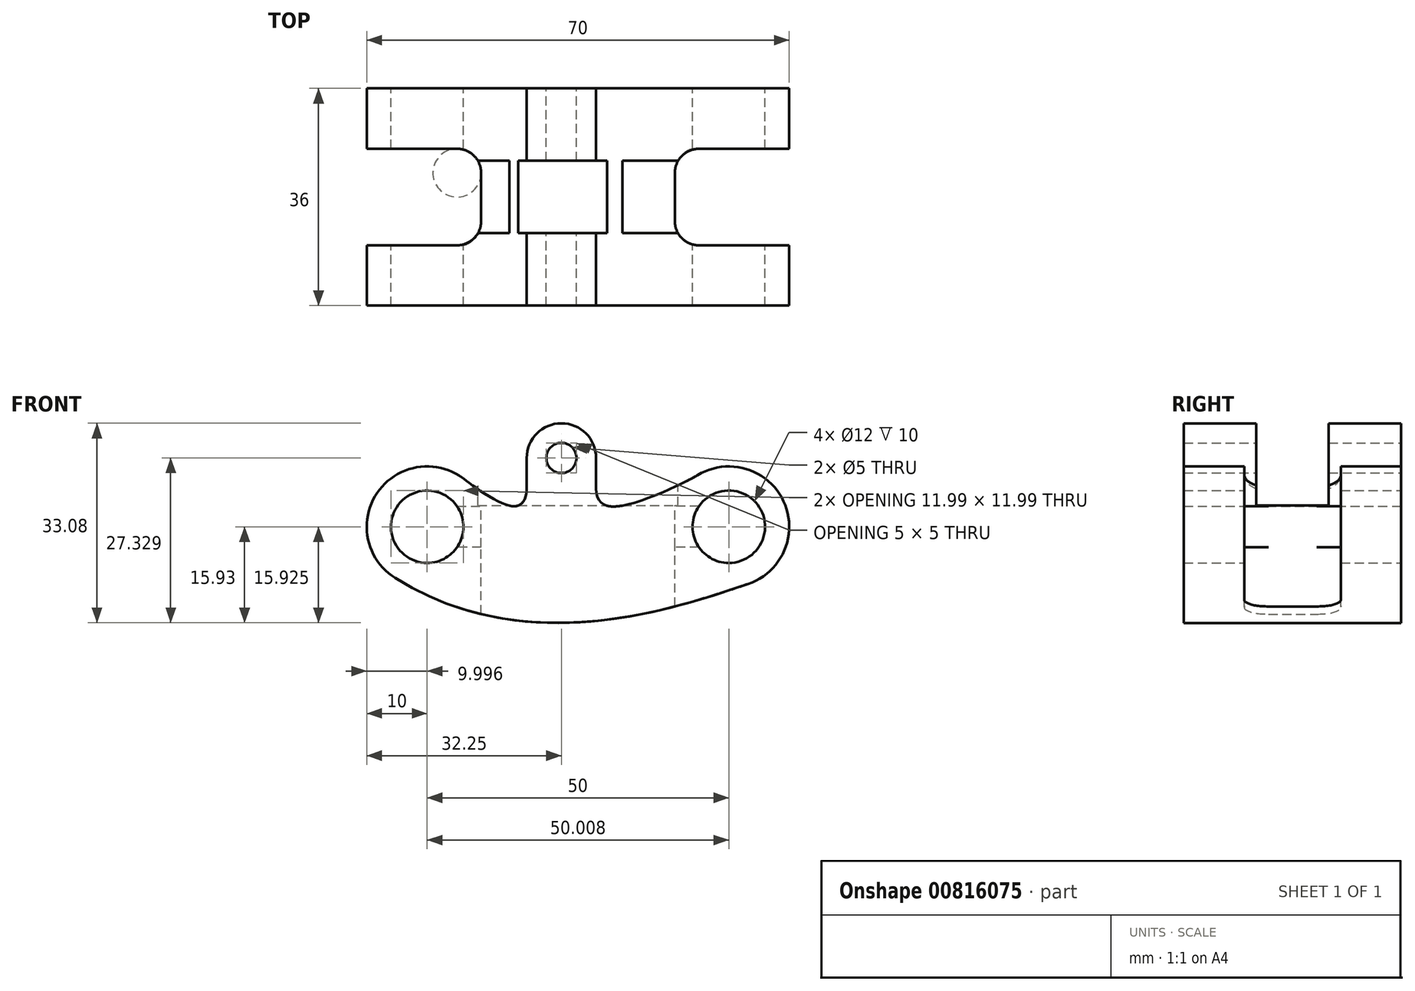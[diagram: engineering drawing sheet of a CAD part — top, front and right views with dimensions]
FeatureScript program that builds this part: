
annotation { "Feature Type Name" : "Feature", "Feature Type Description" : "" }
export const myFeature = defineFeature(function(context is Context, id is Id, definition is map)
    precondition{}
    {
        {
            var Q0;
            Q0=qCreatedBy(makeId("Front.planeOp"),FACE);
            var sketch = newSketch(context, id + "F0", { "sketchPlane" : qUnion([Q0])});
            skCircle(sketch, "E0", {"center": v(-22.25, 0) * mm, "radius": 6 * mm});
            skCircle(sketch, "E1", {"center": v(27.75, 0) * mm, "radius": 6 * mm});
            skCircle(sketch, "E2", {"center": v(0, 11.4) * mm, "radius": 2.5 * mm});
            skSolve(sketch);
        }
        {
            var Q0;
            Q0=qCreatedBy(makeId("Front.planeOp"),FACE);
            var sketch = newSketch(context, id + "F1", { "sketchPlane" : qUnion([Q0])});
            skLineSegment(sketch, "E3", {"start": v(-5.75, 6.2) * mm, "end": v(-5.75, 11.4) * mm});
            skLineSegment(sketch, "E4", {"start": v(5.75, 11.4) * mm, "end": v(5.75, 6.2) * mm});
            skArc(sketch, "E5", {"start": v(5.75, 11.4) * mm, "mid": v(0, 17.15) * mm, "end": v(-5.75, 11.4) * mm});
            skLineSegment(sketch, "E6", {"start": v(-16.87, 11.4) * mm, "end": v(18.4, 11.4) * mm, "construction": true});
            skFitSpline(sketch, "E7", {"points": [v(-16.37, 8.09) * mm, v(-7.6, 3.4) * mm, v(-5.75, 6.2) * mm], "startDerivative": vector(4.71, -3.43) * mm, "endDerivative": vector(0, 8.16) * mm});
            skFitSpline(sketch, "E8", {"points": [v(5.75, 6.2) * mm, v(8, 3.4) * mm, v(22.7, 8.64) * mm], "startDerivative": vector(0, -9.25) * mm, "endDerivative": vector(5.65, 3.73) * mm});
            skArc(sketch, "E9", {"start": v(30.95, -9.47) * mm, "mid": v(36.81, 4.22) * mm, "end": v(22.55, 8.54) * mm});
            skLineSegment(sketch, "E10", {"start": v(27.75, 12.14) * mm, "end": v(27.75, -11.72) * mm, "construction": true});
            skLineSegment(sketch, "E11", {"start": v(-22.25, 15.04) * mm, "end": v(-22.25, -11.72) * mm, "construction": true});
            skArc(sketch, "E12", {"start": v(-16.37, 8.09) * mm, "mid": v(-30.54, 5.6) * mm, "end": v(-27.55, -8.48) * mm});
            skFitSpline(sketch, "E13", {"points": [v(-27.55, -8.48) * mm, v(30.95, -9.47) * mm], "startDerivative": vector(64.39, -40.24) * mm, "endDerivative": vector(40.2, 13.58) * mm});
            skSolve(sketch);
        }
        {
            var Q0;
            Q0 = qSketchRegion(id + "F1", true);
            extrude(context, id + "F2", {"entities" : qUnion([Q0]), "depth" : 36 * mm, "offsetDistance" : 25 * mm});
        }
        {
            var Q0;
            Q0=makeQuery(id+"F0.imprint","IMPRINT",FACE,{"disambiguationData":[TD([[makeQuery(id+"F0.imprint","IMPRINT",EDGE,{"derivedFrom":sQuery(id+"F0.wireOp",EDGE,"E0")}),1.0]])]});
            var Q1;
            Q1=makeQuery(id+"F0.imprint","IMPRINT",FACE,{"disambiguationData":[TD([[makeQuery(id+"F0.imprint","IMPRINT",EDGE,{"derivedFrom":sQuery(id+"F0.wireOp",EDGE,"E2")}),1.0]])]});
            var Q2;
            Q2=makeQuery(id+"F0.imprint","IMPRINT",FACE,{"disambiguationData":[TD([[makeQuery(id+"F0.imprint","IMPRINT",EDGE,{"derivedFrom":sQuery(id+"F0.wireOp",EDGE,"E1")}),1.0]])]});
            var Q3;
            Q3=sQuery(id+"F0.wireOp",EDGE,"E0");
            extrude(context, id + "F3", {"entities" : qUnion([Q0, Q1, Q2]), "operationType" : NewBodyOperationType.REMOVE, "surfaceEntities" : qUnion([Q3]), "depth" : 36 * mm, "offsetDistance" : 25 * mm});
        }
        {
            var Q0;
            Q0=qCreatedBy(makeId("Top.planeOp"),FACE);
            cPlane(context, id + "F4", {"entities" : qUnion([Q0]), "cplaneType" : CPlaneType.OFFSET, "offset" : 3.5 * mm, "width" : 150 * mm, "height" : 150 * mm});
        }
        {
            var Q0;
            Q0=qCreatedBy(id+"F4.planeOp",FACE);
            var sketch = newSketch(context, id + "F5", { "sketchPlane" : qUnion([Q0])});
            skLineSegment(sketch, "E14.bottom", {"start": v(-35, -12) * mm, "end": v(40, -12) * mm});
            skLineSegment(sketch, "E14.top", {"start": v(-35, -24) * mm, "end": v(40, -24) * mm});
            skLineSegment(sketch, "E14.left", {"start": v(-35, -12) * mm, "end": v(-35, -24) * mm});
            skLineSegment(sketch, "E14.right", {"start": v(40, -12) * mm, "end": v(40, -24) * mm});
            skSolve(sketch);
        }
        {
            var Q0;
            Q0 = qSketchRegion(id + "F5", true);
            extrude(context, id + "F6", {"entities" : qUnion([Q0]), "operationType" : NewBodyOperationType.REMOVE, "depth" : 15 * mm, "offsetDistance" : 25 * mm});
        }
        {
            var Q0;
            Q0=qCreatedBy(id+"F4.planeOp",FACE);
            var sketch = newSketch(context, id + "F7", { "sketchPlane" : qUnion([Q0])});
            skLineSegment(sketch, "E15.bottom", {"start": v(37.8, -26) * mm, "end": v(18.8, -26) * mm});
            skLineSegment(sketch, "E15.top", {"start": v(37.8, -10) * mm, "end": v(18.8, -10) * mm});
            skLineSegment(sketch, "E15.left", {"start": v(37.8, -26) * mm, "end": v(37.8, -10) * mm});
            skLineSegment(sketch, "E15.right", {"start": v(18.8, -26) * mm, "end": v(18.8, -10) * mm});
            skLineSegment(sketch, "E16.bottom", {"start": v(-13.3, -26) * mm, "end": v(-32.3, -26) * mm});
            skLineSegment(sketch, "E16.top", {"start": v(-13.3, -10) * mm, "end": v(-32.3, -10) * mm});
            skLineSegment(sketch, "E16.left", {"start": v(-13.3, -26) * mm, "end": v(-13.3, -10) * mm});
            skLineSegment(sketch, "E16.right", {"start": v(-32.3, -26) * mm, "end": v(-32.3, -10) * mm});
            skSolve(sketch);
        }
        {
            var Q0;
            Q0 = qSketchRegion(id + "F7", true);
            extrude(context, id + "F8", {"entities" : qUnion([Q0]), "operationType" : NewBodyOperationType.REMOVE, "oppositeDirection" : true, "depth" : 20 * mm, "offsetDistance" : 25 * mm});
        }
        {
            var Q0;
            Q0 = qSketchRegion(id + "F7", true);
            extrude(context, id + "F9", {"entities" : qUnion([Q0]), "operationType" : NewBodyOperationType.REMOVE, "depth" : 25 * mm, "offsetDistance" : 25 * mm});
        }
        {
            var Q0;
            {var subQ0=sQuery(id+"F7.wireOp",EDGE,"E15.right");var subQ1=sQuery(id+"F7.wireOp",EDGE,"E15.bottom");Q0=makeQuery(id+"F9.boolean.opBoolean","MERGE",EDGE,{"derivedFrom":[makeQuery(id+"F8.boolean.opBoolean","COPY",EDGE,{"derivedFrom":makeQuery(id+"F8.opExtrude","SWEPT_EDGE",EDGE,{"disambiguationData":[OSD([subQ1,subQ0])]})}),makeQuery(id+"F9.opExtrude","SWEPT_EDGE",EDGE,{"disambiguationData":[OSD([subQ1,subQ0])]})]});}
            var Q1;
            {var subQ0=sQuery(id+"F7.wireOp",EDGE,"E15.right");var subQ1=sQuery(id+"F7.wireOp",EDGE,"E15.top");Q1=makeQuery(id+"F9.boolean.opBoolean","MERGE",EDGE,{"derivedFrom":[makeQuery(id+"F8.boolean.opBoolean","COPY",EDGE,{"derivedFrom":makeQuery(id+"F8.opExtrude","SWEPT_EDGE",EDGE,{"disambiguationData":[OSD([subQ1,subQ0])]})}),makeQuery(id+"F9.opExtrude","SWEPT_EDGE",EDGE,{"disambiguationData":[OSD([subQ1,subQ0])]})]});}
            var Q2;
            {var subQ0=sQuery(id+"F7.wireOp",EDGE,"E16.left");var subQ1=sQuery(id+"F7.wireOp",EDGE,"E16.top");Q2=makeQuery(id+"F9.boolean.opBoolean","MERGE",EDGE,{"derivedFrom":[makeQuery(id+"F8.boolean.opBoolean","COPY",EDGE,{"derivedFrom":makeQuery(id+"F8.opExtrude","SWEPT_EDGE",EDGE,{"disambiguationData":[OSD([subQ1,subQ0])]})}),makeQuery(id+"F9.opExtrude","SWEPT_EDGE",EDGE,{"disambiguationData":[OSD([subQ1,subQ0])]})]});}
            var Q3;
            {var subQ0=sQuery(id+"F7.wireOp",EDGE,"E16.left");var subQ1=sQuery(id+"F7.wireOp",EDGE,"E16.bottom");Q3=makeQuery(id+"F9.boolean.opBoolean","MERGE",EDGE,{"derivedFrom":[makeQuery(id+"F8.boolean.opBoolean","COPY",EDGE,{"derivedFrom":makeQuery(id+"F8.opExtrude","SWEPT_EDGE",EDGE,{"disambiguationData":[OSD([subQ1,subQ0])]})}),makeQuery(id+"F9.opExtrude","SWEPT_EDGE",EDGE,{"disambiguationData":[OSD([subQ1,subQ0])]})]});}
            fillet(context, id + "F10", {"entities" : qUnion([Q0, Q1, Q2, Q3]), "radius" : 4 * mm, "tangentPropagation" : true, "allowEdgeOverflow" : false});
        }
    });
